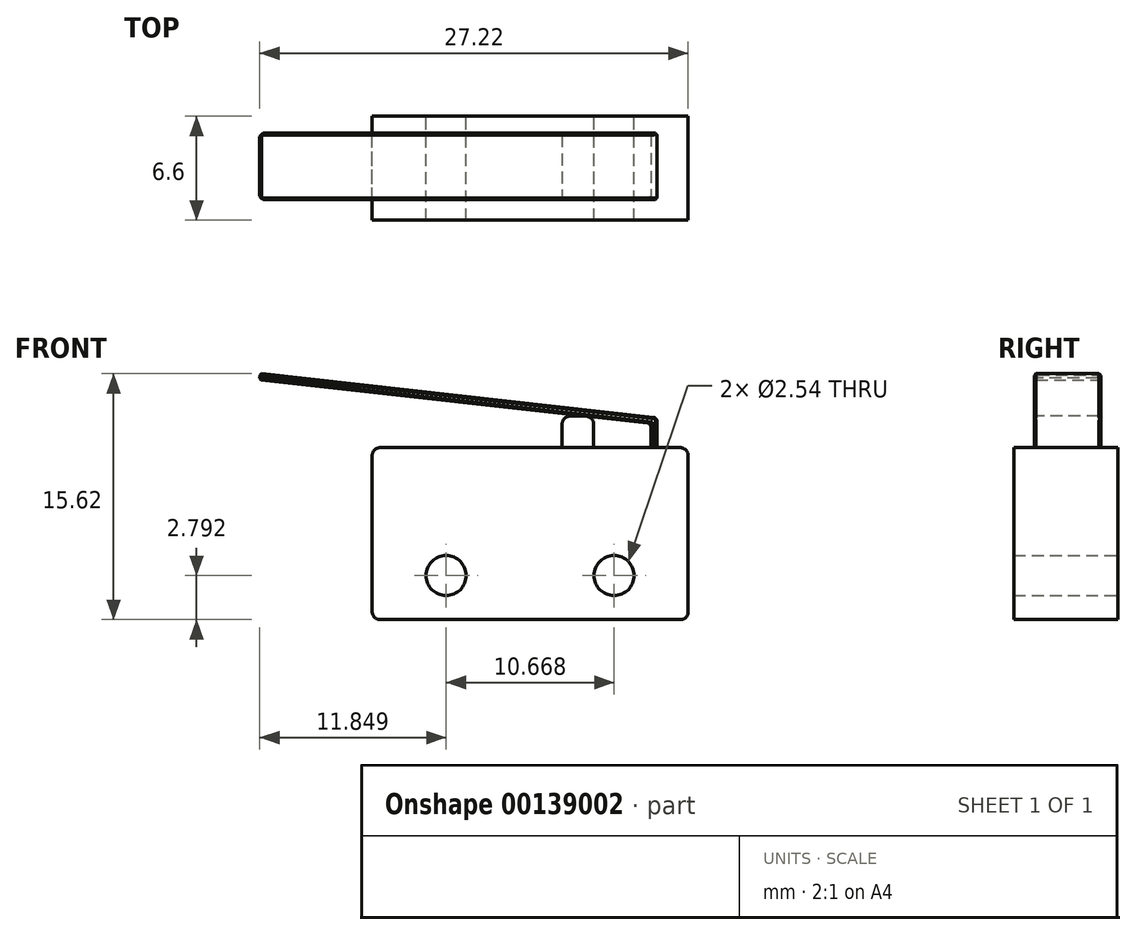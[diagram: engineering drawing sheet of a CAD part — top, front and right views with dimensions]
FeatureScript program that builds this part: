
annotation { "Feature Type Name" : "Feature", "Feature Type Description" : "" }
export const myFeature = defineFeature(function(context is Context, id is Id, definition is map)
    precondition{}
    {
        {
            var Q0;
            Q0=qCreatedBy(makeId("Front.planeOp"),FACE);
            var sketch = newSketch(context, id + "F0", { "sketchPlane" : qUnion([Q0])});
            skLineSegment(sketch, "E0.bottom", {"start": v(0, 0) * mm, "end": v(20.07, 0) * mm});
            skLineSegment(sketch, "E0.top", {"start": v(0, -10.92) * mm, "end": v(20.07, -10.92) * mm});
            skLineSegment(sketch, "E0.left", {"start": v(0, 0) * mm, "end": v(0, -10.92) * mm});
            skLineSegment(sketch, "E0.right", {"start": v(20.07, 0) * mm, "end": v(20.07, -10.92) * mm});
            skLineSegment(sketch, "E1", {"start": v(0, -8.13) * mm, "end": v(20.07, -8.13) * mm, "construction": true});
            skPoint(sketch, "E2", {"position": v(10.03, -8.13) * mm});
            skCircle(sketch, "E3", {"center": v(4.7, -8.13) * mm, "radius": 1.27 * mm});
            skCircle(sketch, "E4", {"center": v(15.37, -8.13) * mm, "radius": 1.27 * mm});
            skSolve(sketch);
        }
        {
            var Q0;
            Q0 = qSketchRegion(id + "F0", true);
            extrude(context, id + "F1", {"entities" : qUnion([Q0]), "depth" : 6.6 * mm});
        }
        {
            var Q0;
            Q0=makeQuery(id+"F1.opExtrude","SWEPT_FACE",FACE,{"disambiguationData":[OSD([sQuery(id+"F0.wireOp",EDGE,"E0.bottom")])]});
            var sketch = newSketch(context, id + "F2", { "sketchPlane" : qUnion([Q0])});
            skLineSegment(sketch, "E5.bottom", {"start": v(12.07, -1.22) * mm, "end": v(14.07, -1.22) * mm});
            skLineSegment(sketch, "E5.top", {"start": v(12.07, -5.28) * mm, "end": v(14.07, -5.28) * mm});
            skLineSegment(sketch, "E5.left", {"start": v(12.07, -1.22) * mm, "end": v(12.07, -5.28) * mm});
            skLineSegment(sketch, "E5.right", {"start": v(14.07, -1.22) * mm, "end": v(14.07, -5.28) * mm});
            skSolve(sketch);
        }
        {
            var Q0;
            Q0 = qSketchRegion(id + "F2", true);
            extrude(context, id + "F3", {"entities" : qUnion([Q0]), "operationType" : NewBodyOperationType.ADD, "depth" : 2 * mm});
        }
        {
            var Q0;
            Q0=makeQuery(id+"F3.opExtrude","CAP_EDGE",EDGE,{"disambiguationData":[OSD([sQuery(id+"F2.wireOp",EDGE,"E5.left")])],"isStart":false});
            var Q1;
            Q1=makeQuery(id+"F3.opExtrude","CAP_EDGE",EDGE,{"disambiguationData":[OSD([sQuery(id+"F2.wireOp",EDGE,"E5.right")])],"isStart":false});
            var Q2;
            Q2=makeQuery(id+"F1.opExtrude","SWEPT_EDGE",EDGE,{"disambiguationData":[OSD([sQuery(id+"F0.wireOp",EDGE,"E0.bottom"),sQuery(id+"F0.wireOp",EDGE,"E0.left")])]});
            var Q3;
            Q3=makeQuery(id+"F1.opExtrude","SWEPT_EDGE",EDGE,{"disambiguationData":[OSD([sQuery(id+"F0.wireOp",EDGE,"E0.bottom"),sQuery(id+"F0.wireOp",EDGE,"E0.right")])]});
            var Q4;
            Q4=makeQuery(id+"F1.opExtrude","SWEPT_EDGE",EDGE,{"disambiguationData":[OSD([sQuery(id+"F0.wireOp",EDGE,"E0.top"),sQuery(id+"F0.wireOp",EDGE,"E0.left")])]});
            var Q5;
            Q5=makeQuery(id+"F1.opExtrude","SWEPT_EDGE",EDGE,{"disambiguationData":[OSD([sQuery(id+"F0.wireOp",EDGE,"E0.top"),sQuery(id+"F0.wireOp",EDGE,"E0.right")])]});
            fillet(context, id + "F4", {"entities" : qUnion([Q0, Q1, Q2, Q3, Q4, Q5]), "radius" : .5 * mm, "tangentPropagation" : true, "allowEdgeOverflow" : false});
        }
        {
            var Q0;
            Q0=makeQuery(id+"F1.opExtrude","SWEPT_FACE",FACE,{"disambiguationData":[OSD([sQuery(id+"F0.wireOp",EDGE,"E0.bottom")])]});
            var sketch = newSketch(context, id + "F5", { "sketchPlane" : qUnion([Q0])});
            skLineSegment(sketch, "E6.bottom", {"start": v(17.7, -1.2) * mm, "end": v(18.09, -1.2) * mm});
            skLineSegment(sketch, "E6.top", {"start": v(17.7, -5.4) * mm, "end": v(18.09, -5.4) * mm});
            skLineSegment(sketch, "E6.left", {"start": v(17.7, -1.2) * mm, "end": v(17.7, -5.4) * mm});
            skLineSegment(sketch, "E6.right", {"start": v(18.09, -1.2) * mm, "end": v(18.09, -5.4) * mm});
            skSolve(sketch);
        }
        {
            var Q0;
            Q0=makeQuery(id+"F3.opExtrude","SWEPT_FACE",FACE,{"disambiguationData":[OSD([sQuery(id+"F2.wireOp",EDGE,"E5.top")])]});
            var sketch = newSketch(context, id + "F6", { "sketchPlane" : qUnion([Q0])});
            skLineSegment(sketch, "E7.0", {"start": v(18.09, 1.5) * mm, "end": v(18.09, 0) * mm});
            skLineSegment(sketch, "E8", {"start": v(18.09, 1.5) * mm, "end": v(-7.16, 4.3) * mm});
            skLineSegment(sketch, "E9", {"start": v(-7.16, 4.3) * mm, "end": v(-7.11, 4.7) * mm});
            skLineSegment(sketch, "E10", {"start": v(-7.11, 4.7) * mm, "end": v(18.09, 1.9) * mm});
            skLineSegment(sketch, "E11", {"start": v(18.09, 1.9) * mm, "end": v(18.09, 1.5) * mm});
            skPoint(sketch, "E12.0", {"position": v(17.7, 0) * mm});
            skLineSegment(sketch, "E13", {"start": v(18.09, 0) * mm, "end": v(17.7, 0) * mm});
            skLineSegment(sketch, "E14", {"start": v(17.7, 0) * mm, "end": v(17.7, 1.54) * mm});
            skSolve(sketch);
        }
        {
            var Q0;
            {var subQ0=sQuery(id+"F6.wireOp",EDGE,"E7.0");Q0=makeQuery(id+"F6.imprint","IMPRINT",FACE,{"disambiguationData":[TD([[makeQuery(id+"F6.imprint","IMPRINT",EDGE,{"derivedFrom":subQ0}),-1.0]])]});}
            var Q1;
            {var subQ0=sQuery(id+"F6.wireOp",EDGE,"E9");Q1=makeQuery(id+"F6.imprint","IMPRINT",FACE,{"disambiguationData":[TD([[makeQuery(id+"F6.imprint","IMPRINT",EDGE,{"derivedFrom":subQ0}),-1.0]])]});}
            extrude(context, id + "F7", {"entities" : qUnion([Q0, Q1]), "oppositeDirection" : true, "depth" : 4.2 * mm});
        }
        {
            var Q0;
            Q0=makeQuery(id+"F7.opExtrude","CAP_EDGE",EDGE,{"disambiguationData":[OSD([sQuery(id+"F6.wireOp",EDGE,"E7.0"),sQuery(id+"F6.wireOp",EDGE,"E11")])],"isStart":true});
            var Q1;
            Q1=makeQuery(id+"F7.opExtrude","CAP_EDGE",EDGE,{"disambiguationData":[OSD([sQuery(id+"F6.wireOp",EDGE,"E10")])],"isStart":true});
            var Q2;
            Q2=makeQuery(id+"F7.opExtrude","CAP_EDGE",EDGE,{"disambiguationData":[OSD([sQuery(id+"F6.wireOp",EDGE,"E8")])],"isStart":true});
            var Q3;
            Q3=makeQuery(id+"F7.opExtrude","CAP_EDGE",EDGE,{"disambiguationData":[OSD([sQuery(id+"F6.wireOp",EDGE,"E14")])],"isStart":true});
            var Q4;
            Q4=makeQuery(id+"F7.opExtrude","CAP_EDGE",EDGE,{"disambiguationData":[OSD([sQuery(id+"F6.wireOp",EDGE,"E7.0"),sQuery(id+"F6.wireOp",EDGE,"E11")])],"isStart":false});
            var Q5;
            Q5=makeQuery(id+"F7.opExtrude","CAP_EDGE",EDGE,{"disambiguationData":[OSD([sQuery(id+"F6.wireOp",EDGE,"E10")])],"isStart":false});
            var Q6;
            Q6=makeQuery(id+"F7.opExtrude","CAP_EDGE",EDGE,{"disambiguationData":[OSD([sQuery(id+"F6.wireOp",EDGE,"E14")])],"isStart":false});
            var Q7;
            Q7=makeQuery(id+"F7.opExtrude","CAP_EDGE",EDGE,{"disambiguationData":[OSD([sQuery(id+"F6.wireOp",EDGE,"E8")])],"isStart":false});
            var Q8;
            Q8=makeQuery(id+"F7.opExtrude","SWEPT_EDGE",EDGE,{"disambiguationData":[OSD([sQuery(id+"F6.wireOp",EDGE,"E9"),sQuery(id+"F6.wireOp",EDGE,"E10")])]});
            var Q9;
            Q9=makeQuery(id+"F7.opExtrude","SWEPT_EDGE",EDGE,{"disambiguationData":[OSD([sQuery(id+"F6.wireOp",EDGE,"E8"),sQuery(id+"F6.wireOp",EDGE,"E9")])]});
            chamfer(context, id + "F8", {"entities" : qUnion([Q0, Q1, Q2, Q3, Q4, Q5, Q6, Q7, Q8, Q9]), "width" : .1 * mm, "tangentPropagation" : true});
        }
        {
            var Q0;
            Q0=makeQuery(id+"F7.opExtrude","CAP_EDGE",EDGE,{"disambiguationData":[OSD([sQuery(id+"F6.wireOp",EDGE,"E9")])],"isStart":true});
            var Q1;
            Q1=makeQuery(id+"F7.opExtrude","CAP_EDGE",EDGE,{"disambiguationData":[OSD([sQuery(id+"F6.wireOp",EDGE,"E9")])],"isStart":false});
            chamfer(context, id + "F9", {"entities" : qUnion([Q0, Q1]), "width" : .2 * mm, "tangentPropagation" : true});
        }
        {
            var Q0;
            Q0=makeQuery(id+"F7.opExtrude","SWEPT_EDGE",EDGE,{"disambiguationData":[OSD([sQuery(id+"F6.wireOp",EDGE,"E8"),sQuery(id+"F6.wireOp",EDGE,"E14")])]});
            var Q1;
            Q1=makeQuery(id+"F7.opExtrude","SWEPT_EDGE",EDGE,{"disambiguationData":[OSD([sQuery(id+"F6.wireOp",EDGE,"E10"),sQuery(id+"F6.wireOp",EDGE,"E11")])]});
            fillet(context, id + "F10", {"entities" : qUnion([Q0, Q1]), "radius" : .25 * mm, "tangentPropagation" : true, "allowEdgeOverflow" : false});
        }
    });
